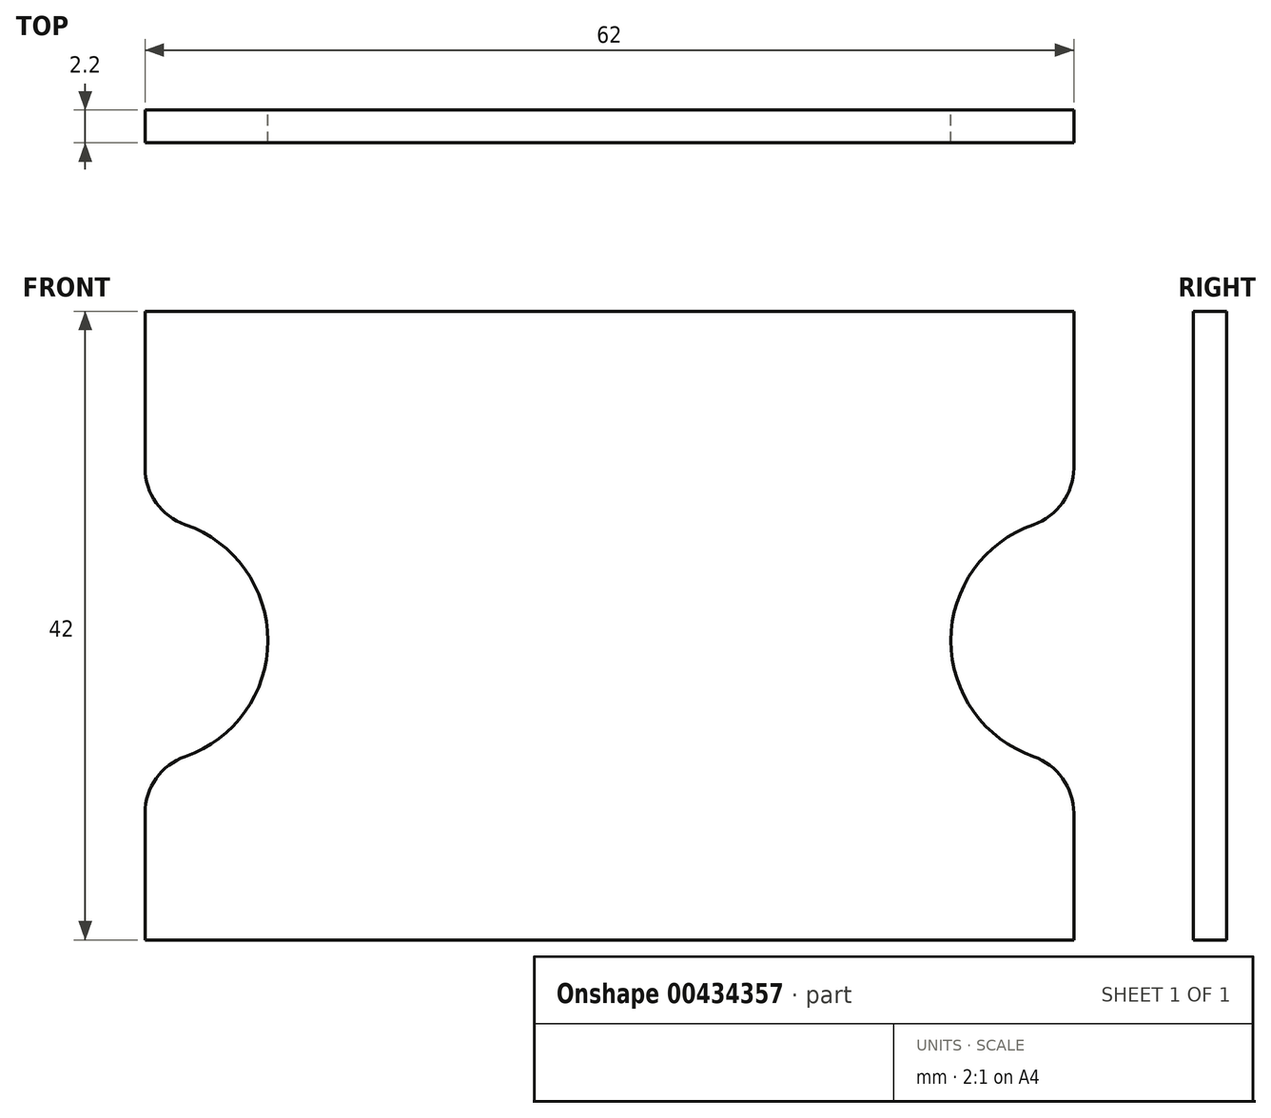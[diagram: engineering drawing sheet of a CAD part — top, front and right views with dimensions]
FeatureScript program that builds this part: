
annotation { "Feature Type Name" : "Feature", "Feature Type Description" : "" }
export const myFeature = defineFeature(function(context is Context, id is Id, definition is map)
    precondition{}
    {
        {
            var Q0;
            Q0=qCreatedBy(makeId("Front.planeOp"),FACE);
            var sketch = newSketch(context, id + "F0", { "sketchPlane" : qUnion([Q0])});
            skLineSegment(sketch, "E0", {"start": v(31, 0) * mm, "end": v(31, 11.8) * mm});
            skLineSegment(sketch, "E1", {"start": v(0, -44.96) * mm, "end": v(0, 184.97) * mm, "construction": true});
            skLineSegment(sketch, "E2.MirrorCS", {"start": v(-31, 0) * mm, "end": v(-31, 11.8) * mm});
            skLineSegment(sketch, "E3", {"start": v(-41.06, 20) * mm, "end": v(53, 20) * mm, "construction": true});
            skArc(sketch, "E4", {"start": v(31, 28.2) * mm, "mid": v(22.8, 20) * mm, "end": v(31, 11.8) * mm});
            skArc(sketch, "E5", {"start": v(-31, 28.2) * mm, "mid": v(-22.8, 20) * mm, "end": v(-31, 11.8) * mm});
            skPoint(sketch, "E6.MirrorP", {"position": v(0, 86) * mm});
            skLineSegment(sketch, "E7", {"start": v(31, 28.2) * mm, "end": v(31, 42) * mm});
            skLineSegment(sketch, "E8", {"start": v(31, 42) * mm, "end": v(-31, 42) * mm});
            skLineSegment(sketch, "E9", {"start": v(-31, 28.2) * mm, "end": v(-31, 42) * mm});
            skLineSegment(sketch, "E10", {"start": v(31, 0) * mm, "end": v(-31, 0) * mm});
            skLineSegment(sketch, "E11", {"start": v(-47.2, 0) * mm, "end": v(55.92, 0) * mm, "construction": true});
            skSolve(sketch);
        }
        {
            var Q0;
            Q0=qSketchRegion(id+"F0",true);
            extrude(context, id + "F1", {"entities" : qUnion([Q0]), "depth" : 2.2 * mm});
        }
        {
            var Q0;
            Q0=makeQuery(id+"F1.opExtrude","SWEPT_EDGE",EDGE,{"disambiguationData":[OSD([sQuery(id+"F0.wireOp",EDGE,"E5"),sQuery(id+"F0.wireOp",EDGE,"0aebadc9-47d1-4a55-8ed3-6b3125491064.trimOffspring")])]});
            var Q1;
            Q1=makeQuery(id+"F1.opExtrude","SWEPT_EDGE",EDGE,{"disambiguationData":[OSD([sQuery(id+"F0.wireOp",EDGE,"E2.MirrorCS"),sQuery(id+"F0.wireOp",EDGE,"E5")])]});
            var Q2;
            Q2=makeQuery(id+"F1.opExtrude","SWEPT_EDGE",EDGE,{"disambiguationData":[OSD([sQuery(id+"F0.wireOp",EDGE,"E0"),sQuery(id+"F0.wireOp",EDGE,"E4")])]});
            var Q3;
            Q3=makeQuery(id+"F1.opExtrude","SWEPT_EDGE",EDGE,{"disambiguationData":[OSD([sQuery(id+"F0.wireOp",EDGE,"E4"),sQuery(id+"F0.wireOp",EDGE,"c0cafa30-3cae-44b1-b917-c793e0f70624.trimOffspring")])]});
            fillet(context, id + "F2", {"entities" : qUnion([Q0, Q1, Q2, Q3]), "radius" : 4 * mm, "tangentPropagation" : true, "allowEdgeOverflow" : false});
        }
    });
